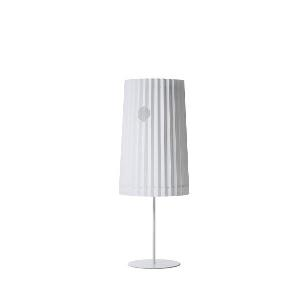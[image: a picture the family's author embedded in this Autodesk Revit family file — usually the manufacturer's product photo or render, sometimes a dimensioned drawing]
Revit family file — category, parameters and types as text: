
# Revit family: vivaa_social_-_vss_7000_vtl_d_ws_985mm_rws_00816399_1ac2
name_source: partatom
category: Lighting Fixtures
units: mm (PartAtom-declared; Revit-internal decimal feet)

## family parameters
Cut with Voids When Loaded = No
Host = Face
Light Source = No
Part Type = Normal
Room Calculation Point = No
Round Connector Dimension = Use Diameter
Shared = No

## types (1)
- VIVAA.social - VSS 7000/VTL/D/WS/985MM/RWS (1 x LED, 7050 lm, 2700-6500K)
    Apparent Load = 79 VA
    Approval mark = CE
    CIE Flux Codes = 46 69 86 24 100
    Color Rendering = 90-100
    Color Temperature = 2700-6500K
    Control Gear = Electronic ballast
    Default Elevation = 1800 mm
    Description = VSS 7000/VTL/D|Free-standing luminaire|light source:     |work equipment: Electronic ballast|light distribution: Direct/indirect|direct ratio: approx. 24 %|technology: Continuously dimmable|operation: Pull cord|luminaire body|material: glass fiber/cellulose|surface: Untreated|colour: Nature|lamp cover: Polycarbonate (PC), Satine|tubular section|material: Steel tube|surface: Painted|Form: Tubular section upright|colour of tubular section: Pure white|luminaire base|Form: Round (flat)|mains lead: 2.20 m Mains plug CEE 7/VII|Fastening: Floor standing base|glare control: Diffusor|
    Frequency = 60 Hz
    Height = 985 mm
    Lamp = 1 x LED
    Lamp Light Flux = 7050 lm
    Lamp count = 1
    Length = 609 mm
    Luminous efficacy = 89 lm/W
    Manufacturer = Waldmann
    ModVariant = No
    Model = 00816399
    Mounting Place = Floor
    Mounting Type = Freestanding
    Number of Poles = 1
    OnlyDefault = Yes
    Power Factor = 1
    Product Name = VIVAA.social - VSS 7000/VTL/D/WS/985MM/RWS
    Product group = Free standing luminaire
    ProductGroupID = 13
    Protection Class = Protection class I
    Protection Degree = IP 20
    RLX_Detail_Level = 1
    RLX_Emergency_Light_Flux = 0 lm
    RLX_Emergency_Type = 0
    RLX_Emergency_Type_DB = No
    RlxData = <blob elided: 72197 chars, md5=9370871a>
    Socket = socket
    Standby Power = 0 W
    System Light Flux = 7050 lm
    System Power = 79 W
    Type Comments = Product without accessories
    Type Image = vivaasocial_weiss_kurz.jpg
    URL = http://relux.com
    VarID = ---
    Voltage = 230 V
    Voltage Range = 220-240 V
    Weight = 0.00 kg
    Width = 0 mm  [stored 0 ft]

note: [stored X ft] marks values corroborated as IEEE doubles in the binary element streams (Revit-internal decimal feet)

## geometry (parser evidence)
native form markers: Blend x4, Sweep x15
no freeform markers — native parametric forms only
